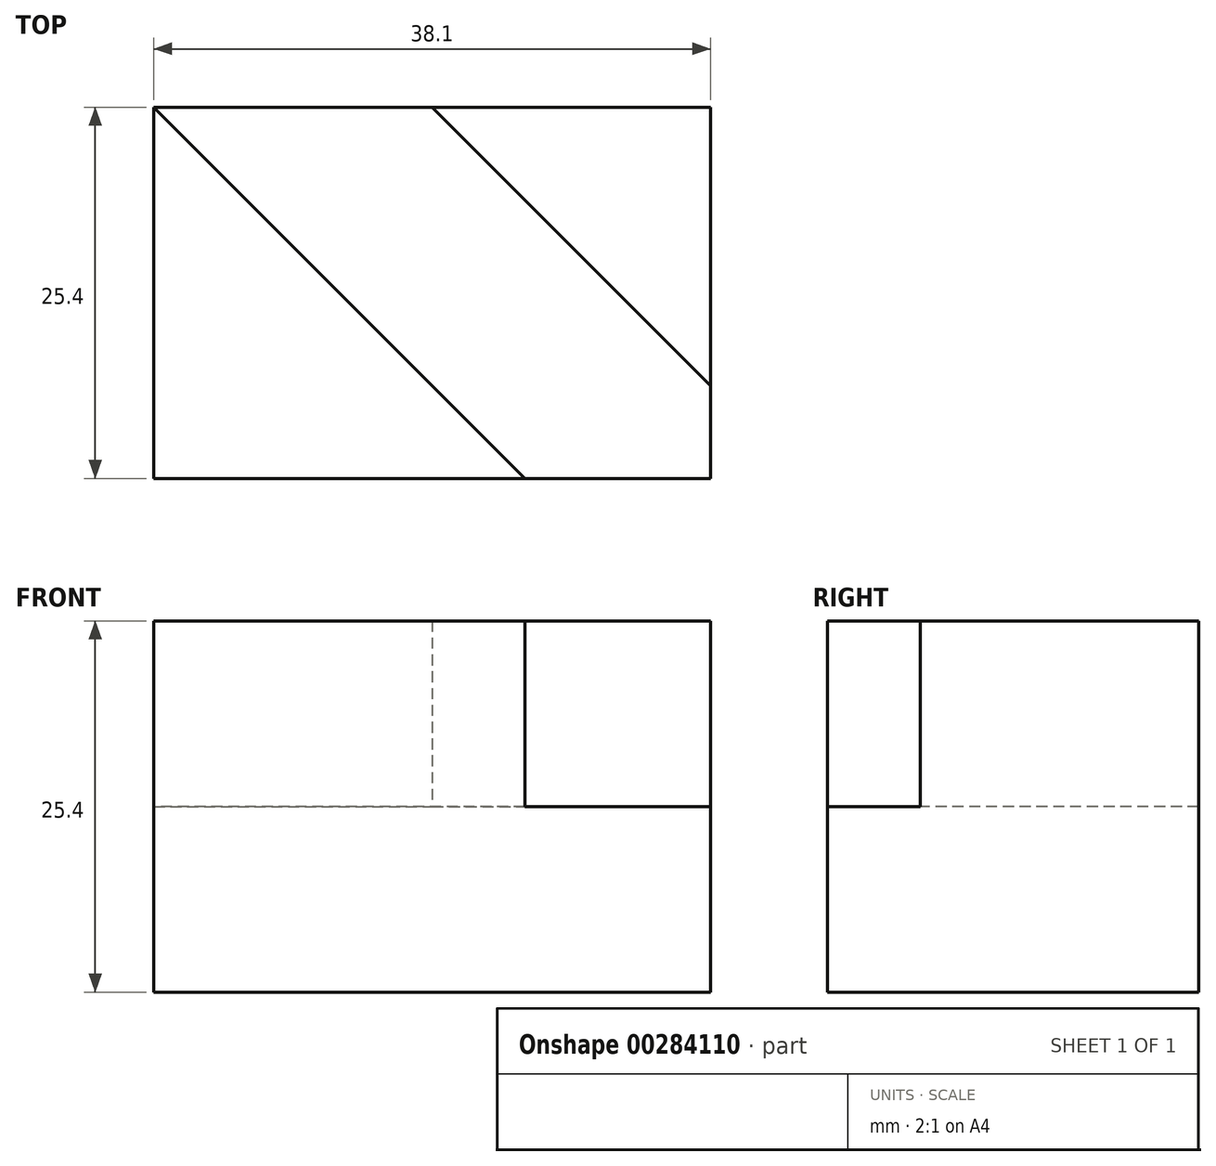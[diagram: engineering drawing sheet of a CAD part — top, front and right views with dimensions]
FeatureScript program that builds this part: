
annotation { "Feature Type Name" : "Feature", "Feature Type Description" : "" }
export const myFeature = defineFeature(function(context is Context, id is Id, definition is map)
    precondition{}
    {
        {
            var Q0;
            Q0=qCreatedBy(makeId("Front.planeOp"),FACE);
            var sketch = newSketch(context, id + "F0", { "sketchPlane" : qUnion([Q0])});
            skLineSegment(sketch, "E0.bottom", {"start": v(0, 0) * mm, "end": v(38.1, 0) * mm});
            skLineSegment(sketch, "E0.top", {"start": v(0, 12.7) * mm, "end": v(38.1, 12.7) * mm});
            skLineSegment(sketch, "E0.left", {"start": v(0, 0) * mm, "end": v(0, 12.7) * mm});
            skLineSegment(sketch, "E0.right", {"start": v(38.1, 0) * mm, "end": v(38.1, 12.7) * mm});
            skSolve(sketch);
        }
        {
            var Q0;
            Q0=makeQuery(id+"F0.imprint","IMPRINT",FACE,{"disambiguationData":[TD([[makeQuery(id+"F0.imprint","IMPRINT",EDGE,{"derivedFrom":sQuery(id+"F0.wireOp",EDGE,"E0.bottom")}),1.0]])]});
            extrude(context, id + "F1", {"entities" : qUnion([Q0]), "depth" : 25.4 * mm});
        }
        {
            var Q0;
            Q0=makeQuery(id+"F1.opExtrude","SWEPT_FACE",FACE,{"disambiguationData":[OSD([sQuery(id+"F0.wireOp",EDGE,"E0.top")])]});
            var sketch = newSketch(context, id + "F2", { "sketchPlane" : qUnion([Q0])});
            skLineSegment(sketch, "E1", {"start": v(0, 0) * mm, "end": v(0, -25.4) * mm});
            skLineSegment(sketch, "E2", {"start": v(0, -25.4) * mm, "end": v(25.4, -25.4) * mm});
            skLineSegment(sketch, "E3", {"start": v(25.4, -25.4) * mm, "end": v(0, 0) * mm});
            skSolve(sketch);
        }
        {
            var Q0;
            Q0 = qSketchRegion(id + "F2", true);
            extrude(context, id + "F3", {"entities" : qUnion([Q0]), "operationType" : NewBodyOperationType.ADD, "depth" : 12.7 * mm});
        }
        {
            var Q0;
            Q0=makeQuery(id+"F1.opExtrude","SWEPT_FACE",FACE,{"disambiguationData":[OSD([sQuery(id+"F0.wireOp",EDGE,"E0.top")])]});
            var sketch = newSketch(context, id + "F4", { "sketchPlane" : qUnion([Q0])});
            skLineSegment(sketch, "E4", {"start": v(19.05, 0) * mm, "end": v(38.1, -19.05) * mm});
            skLineSegment(sketch, "E5", {"start": v(38.1, -19.05) * mm, "end": v(38.1, 0) * mm});
            skLineSegment(sketch, "E6", {"start": v(38.1, 0) * mm, "end": v(19.05, 0) * mm});
            skSolve(sketch);
        }
        {
            var Q0;
            Q0 = qSketchRegion(id + "F4", true);
            extrude(context, id + "F5", {"entities" : qUnion([Q0]), "operationType" : NewBodyOperationType.ADD, "depth" : 12.7 * mm});
        }
    });
